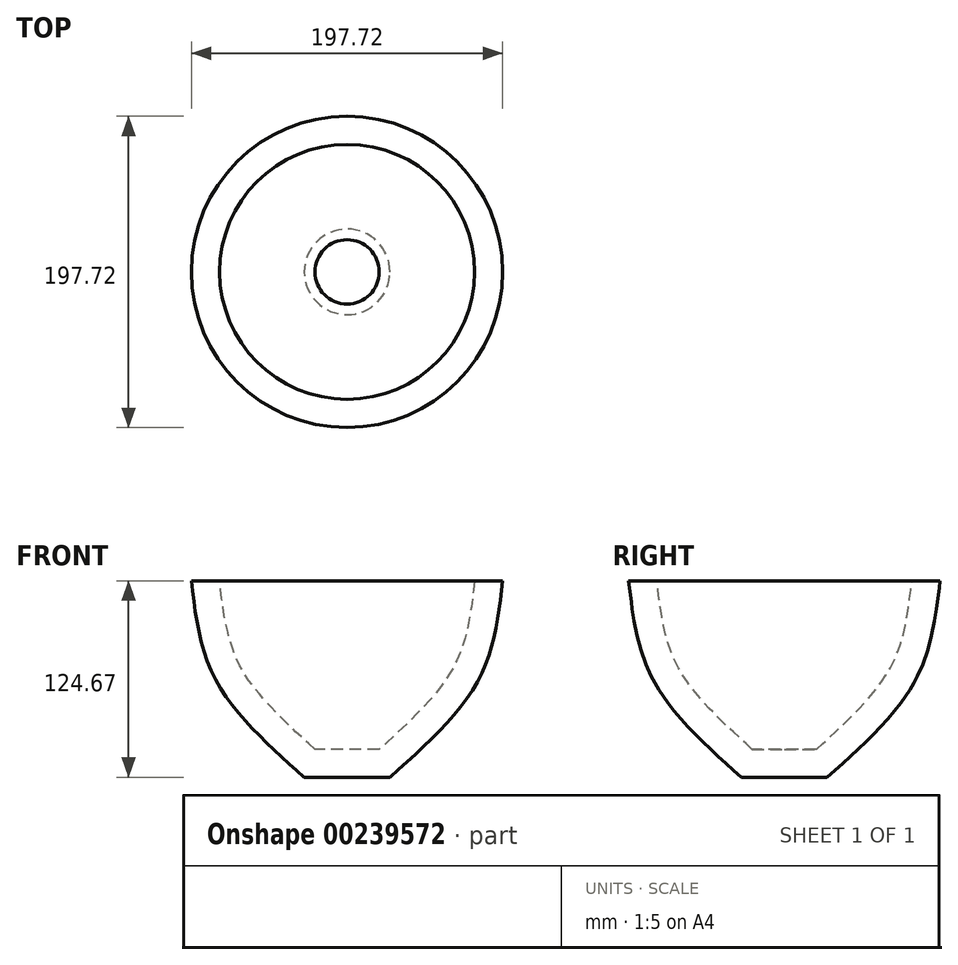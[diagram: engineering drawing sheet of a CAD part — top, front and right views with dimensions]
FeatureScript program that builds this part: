
annotation { "Feature Type Name" : "Feature", "Feature Type Description" : "" }
export const myFeature = defineFeature(function(context is Context, id is Id, definition is map)
    precondition{}
    {
        {
            var Q0;
            Q0=qCreatedBy(makeId("Front.planeOp"),FACE);
            var sketch = newSketch(context, id + "F0", { "sketchPlane" : qUnion([Q0])});
            skLineSegment(sketch, "E0", {"start": v(0, 72.32) * mm, "end": v(-98.86, 72.32) * mm});
            skLineSegment(sketch, "E1", {"start": v(0, 72.32) * mm, "end": v(0, -52.35) * mm});
            skPoint(sketch, "E2.1.internal.orphan", {"position": v(-98.86, 35.84) * mm});
            skLineSegment(sketch, "E3", {"start": v(0, -52.35) * mm, "end": v(-27.21, -52.35) * mm});
            skFitSpline(sketch, "E4", {"points": [v(-98.86, 72.32) * mm, v(-83.45, 9.63) * mm, v(-27.21, -52.35) * mm], "startDerivative": vector(15.97, -138.2) * mm, "endDerivative": vector(124.97, -111.72) * mm});
            skSolve(sketch);
        }
        {
            var Q0;
            Q0 = qSketchRegion(id + "F0", true);
            var Q1;
            Q1=sQuery(id+"F0.wireOp",EDGE,"E1");
            revolve(context, id + "F1", {"entities" : qUnion([Q0]), "axis" : qUnion([Q1]), "revolveType" : RevolveType.FULL});
        }
        {
            var Q0;
            Q0=makeQuery(id+"F1.opRevolve","SWEPT_FACE",FACE,{"disambiguationData":[OSD([sQuery(id+"F0.wireOp",EDGE,"E0")])]});
            shell(context, id + "F2", {"entities" : qUnion([Q0]), "thickness" : 17.78 * mm});
        }
    });
